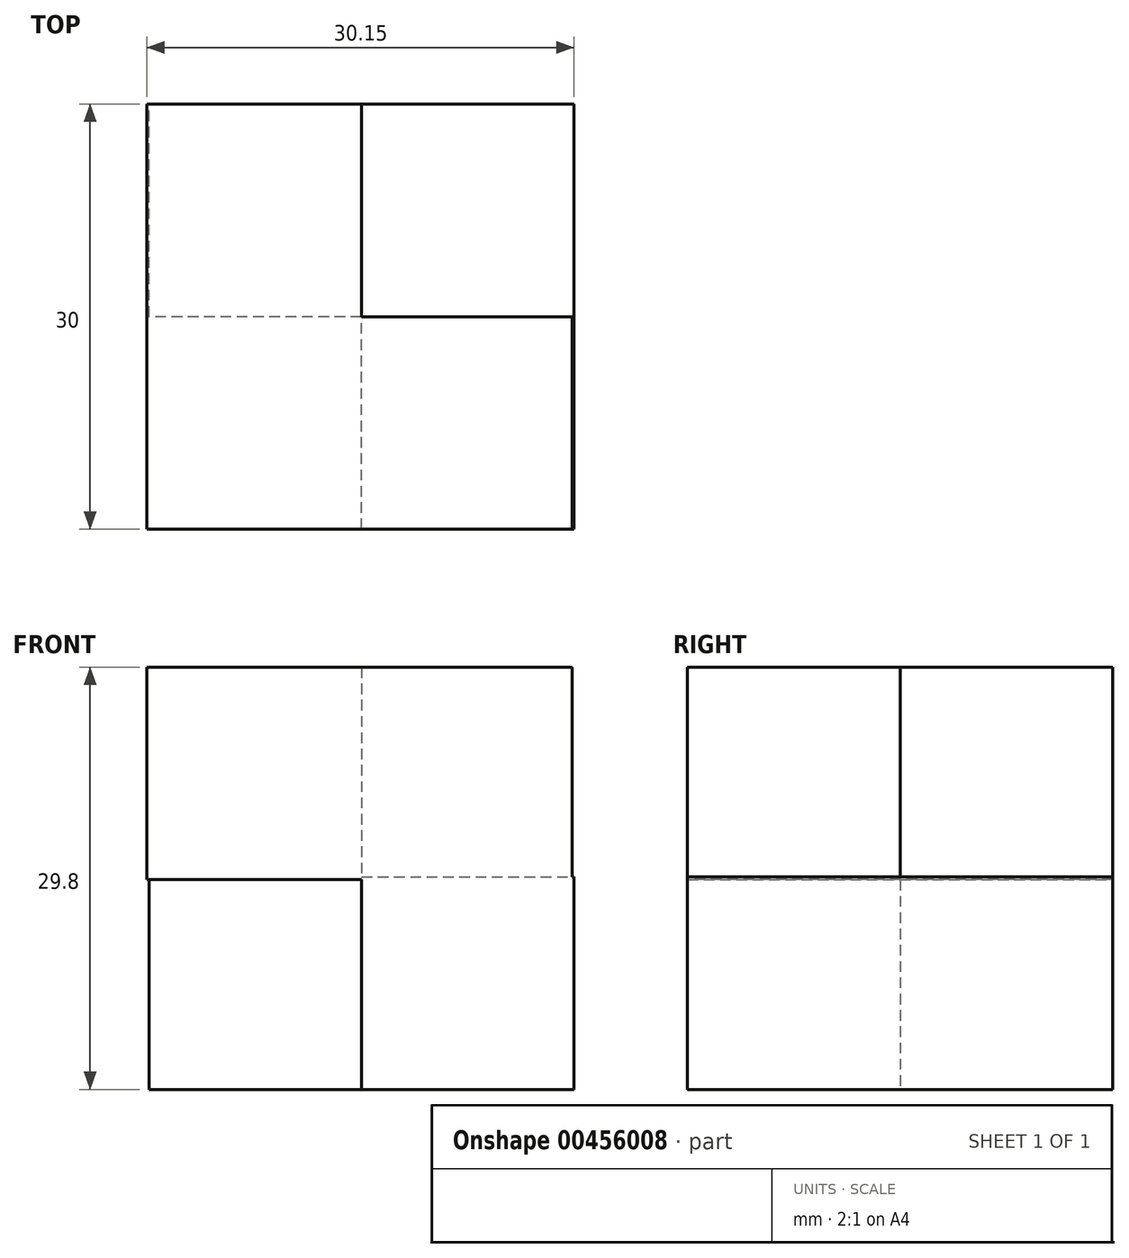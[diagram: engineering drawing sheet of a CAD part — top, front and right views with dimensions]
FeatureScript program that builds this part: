
annotation { "Feature Type Name" : "Feature", "Feature Type Description" : "" }
export const myFeature = defineFeature(function(context is Context, id is Id, definition is map)
    precondition{}
    {
        {
            var Q0;
            Q0=qCreatedBy(makeId("Top.planeOp"),FACE);
            var sketch = newSketch(context, id + "F0", { "sketchPlane" : qUnion([Q0])});
            skLineSegment(sketch, "E0", {"start": v(0, 0) * mm, "end": v(-15, 0) * mm});
            skLineSegment(sketch, "E1", {"start": v(-15, 0) * mm, "end": v(-15, 15) * mm});
            skLineSegment(sketch, "E2", {"start": v(-15, 15) * mm, "end": v(15, 15) * mm});
            skLineSegment(sketch, "E3", {"start": v(15, 15) * mm, "end": v(15, -15) * mm});
            skLineSegment(sketch, "E4", {"start": v(15, -15) * mm, "end": v(0, -15) * mm});
            skLineSegment(sketch, "E5", {"start": v(0, -15) * mm, "end": v(0, 0) * mm});
            skSolve(sketch);
        }
        {
            var Q0;
            Q0=makeQuery(id+"F0.imprint","IMPRINT",FACE,{"disambiguationData":[TD([[makeQuery(id+"F0.imprint","IMPRINT",EDGE,{"derivedFrom":sQuery(id+"F0.wireOp",EDGE,"E0")}),-1.0]])]});
            extrude(context, id + "F1", {"entities" : qUnion([Q0]), "depth" : 15 * mm});
        }
        {
            var Q0;
            Q0=qCreatedBy(makeId("Top.planeOp"),FACE);
            cPlane(context, id + "F2", {"entities" : qUnion([Q0]), "cplaneType" : CPlaneType.OFFSET, "offset" : 14.8 * mm, "width" : 150 * mm, "height" : 150 * mm});
        }
        {
            var Q0;
            Q0=qCreatedBy(id+"F2.planeOp",FACE);
            var sketch = newSketch(context, id + "F3", { "sketchPlane" : qUnion([Q0])});
            skLineSegment(sketch, "E6", {"start": v(0, 0) * mm, "end": v(0, 15) * mm});
            skLineSegment(sketch, "E7", {"start": v(0, 15) * mm, "end": v(-15.15, 15) * mm});
            skLineSegment(sketch, "E8", {"start": v(-15.15, 15) * mm, "end": v(-15.15, -15) * mm});
            skLineSegment(sketch, "E9", {"start": v(-15.15, -15) * mm, "end": v(14.85, -15) * mm});
            skLineSegment(sketch, "E10", {"start": v(14.85, -15) * mm, "end": v(14.85, 0) * mm});
            skLineSegment(sketch, "E11", {"start": v(0, 15) * mm, "end": v(0, 0) * mm});
            skLineSegment(sketch, "E12", {"start": v(14.85, 0) * mm, "end": v(0, 0) * mm});
            skSolve(sketch);
        }
        {
            var Q0;
            Q0 = qSketchRegion(id + "F3", true);
            extrude(context, id + "F4", {"entities" : qUnion([Q0]), "operationType" : NewBodyOperationType.ADD, "depth" : 15 * mm});
        }
    });
